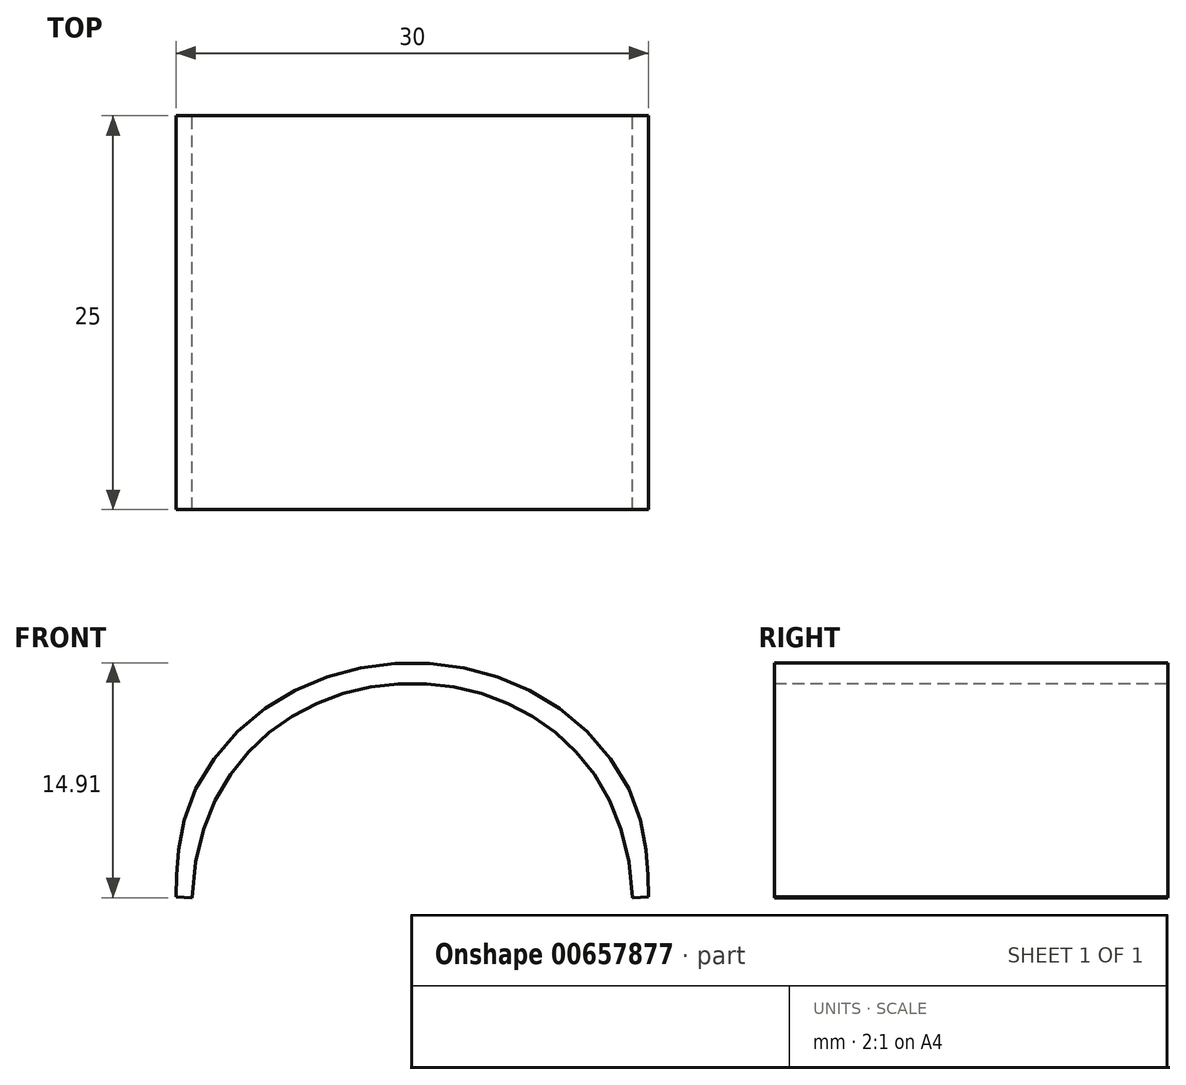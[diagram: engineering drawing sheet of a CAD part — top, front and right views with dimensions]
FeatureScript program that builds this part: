
annotation { "Feature Type Name" : "Feature", "Feature Type Description" : "" }
export const myFeature = defineFeature(function(context is Context, id is Id, definition is map)
    precondition{}
    {
        {
            var Q0;
            Q0=qCreatedBy(makeId("Front.planeOp"),FACE);
            var sketch = newSketch(context, id + "F0", { "sketchPlane" : qUnion([Q0])});
            skFitSpline(sketch, "E0", {"points": [v(-14, 0) * mm, v(14, 0) * mm], "startDerivative": vector(2.08, 54.44) * mm, "endDerivative": vector(2.08, -54.44) * mm});
            skFitSpline(sketch, "E1.0", {"points": [v(-15, 0.04) * mm, v(-14.9, 2.43) * mm, v(-13.86, 6.67) * mm, v(-10.3, 11.27) * mm, v(-5.45, 14) * mm, v(0, 14.91) * mm, v(5.45, 14) * mm, v(10.3, 11.27) * mm, v(13.86, 6.67) * mm, v(14.9, 2.43) * mm, v(15, 0.04) * mm]});
            skLineSegment(sketch, "E2", {"start": v(-15, 0.04) * mm, "end": v(-14, 0) * mm});
            skLineSegment(sketch, "E3", {"start": v(14, 0) * mm, "end": v(15, 0.04) * mm});
            skSolve(sketch);
        }
        {
            var Q0;
            Q0 = qSketchRegion(id + "F0", true);
            extrude(context, id + "F1", {"entities" : qUnion([Q0]), "depth" : 25 * mm, "offsetDistance" : 25 * mm});
        }
    });
